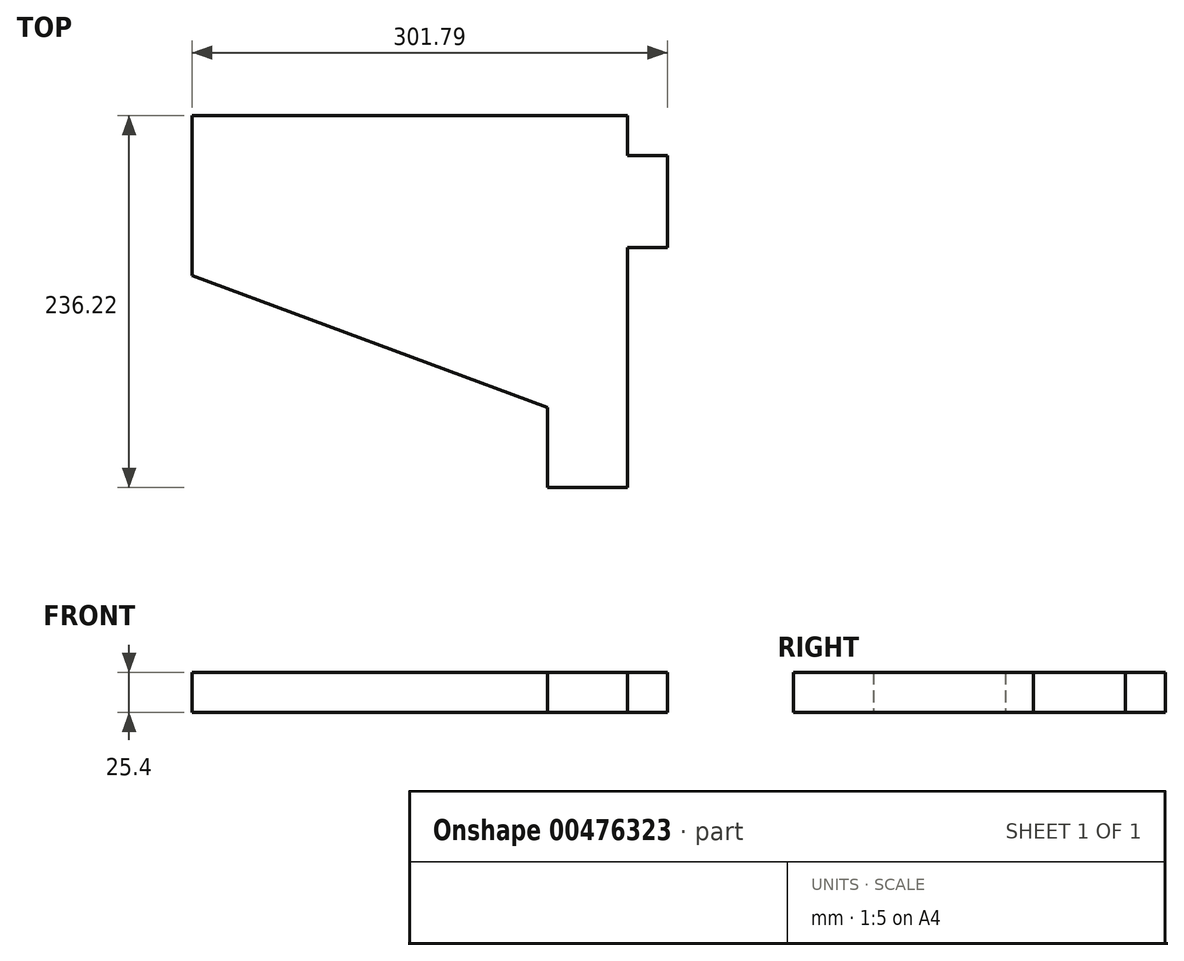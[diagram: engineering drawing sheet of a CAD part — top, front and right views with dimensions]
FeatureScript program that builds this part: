
annotation { "Feature Type Name" : "Feature", "Feature Type Description" : "" }
export const myFeature = defineFeature(function(context is Context, id is Id, definition is map)
    precondition{}
    {
        {
            var Q0;
            Q0=qCreatedBy(makeId("Top.planeOp"),FACE);
            var sketch = newSketch(context, id + "F0", { "sketchPlane" : qUnion([Q0])});
            skLineSegment(sketch, "E0", {"start": v(225.6, -83.82) * mm, "end": v(225.6, -134.62) * mm});
            skLineSegment(sketch, "E1", {"start": v(225.6, -134.62) * mm, "end": v(276.4, -134.62) * mm});
            skLineSegment(sketch, "E2", {"start": v(276.4, -134.62) * mm, "end": v(276.4, 17.78) * mm});
            skLineSegment(sketch, "E3", {"start": v(276.4, 17.78) * mm, "end": v(301.8, 17.78) * mm});
            skLineSegment(sketch, "E4", {"start": v(301.8, 17.78) * mm, "end": v(301.8, 76.2) * mm});
            skLineSegment(sketch, "E5", {"start": v(301.8, 76.2) * mm, "end": v(276.4, 76.2) * mm});
            skLineSegment(sketch, "E6", {"start": v(276.4, 76.2) * mm, "end": v(276.4, 101.6) * mm});
            skLineSegment(sketch, "E7", {"start": v(276.4, 101.6) * mm, "end": v(0, 101.6) * mm});
            skLineSegment(sketch, "E8", {"start": v(0, 101.6) * mm, "end": v(0, 0) * mm});
            skLineSegment(sketch, "E9", {"start": v(0, 0) * mm, "end": v(225.6, -83.82) * mm});
            skSolve(sketch);
        }
        {
            var Q0;
            Q0 = qSketchRegion(id + "F0", true);
            extrude(context, id + "F1", {"entities" : qUnion([Q0]), "depth" : 25.4 * mm});
        }
    });
